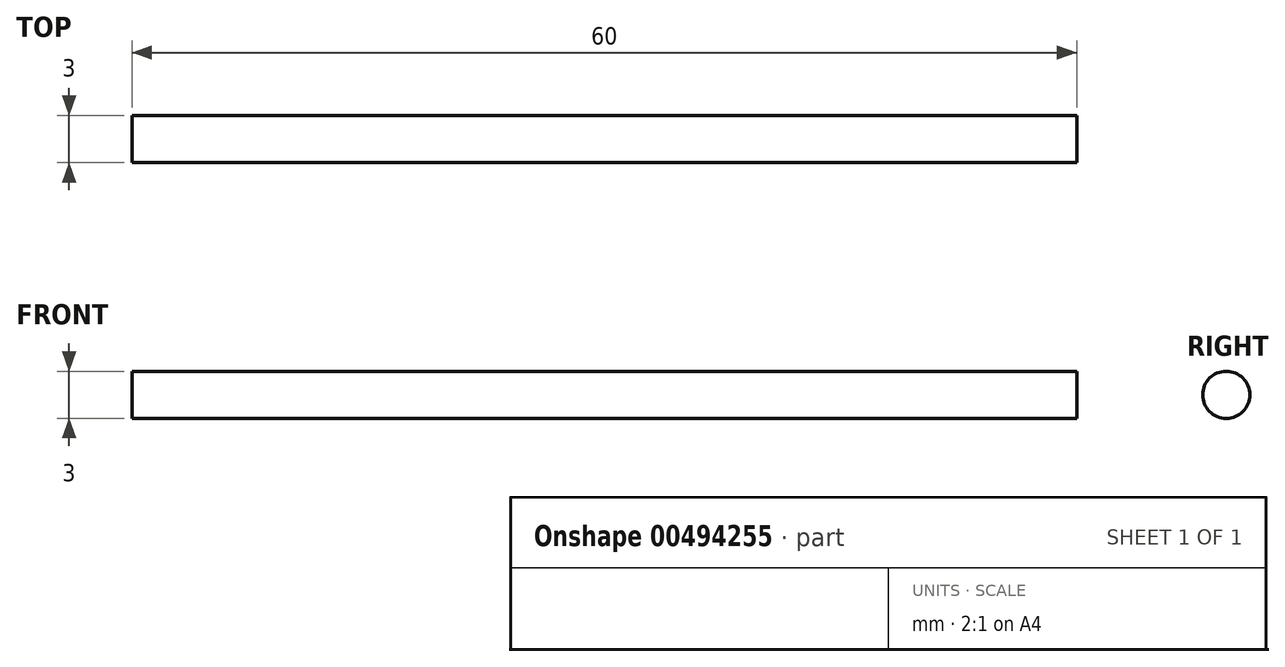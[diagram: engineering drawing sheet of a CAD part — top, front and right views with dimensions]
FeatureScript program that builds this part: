
annotation { "Feature Type Name" : "Feature", "Feature Type Description" : "" }
export const myFeature = defineFeature(function(context is Context, id is Id, definition is map)
    precondition{}
    {
        {
            var Q0;
            Q0=qCreatedBy(makeId("Right.planeOp"),FACE);
            var sketch = newSketch(context, id + "F0", { "sketchPlane" : qUnion([Q0])});
            skCircle(sketch, "E0", {"center": v(0, 0) * mm, "radius": 1.5 * mm});
            skSolve(sketch);
        }
        {
            var Q0;
            Q0 = qSketchRegion(id + "F0", true);
            extrude(context, id + "F1", {"entities" : qUnion([Q0]), "depth" : 60 * mm, "offsetDistance" : 25 * mm, "symmetric" : true});
        }
    });
